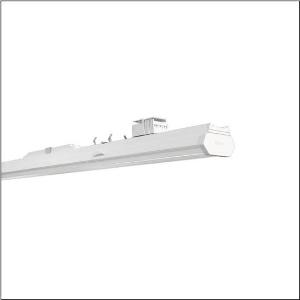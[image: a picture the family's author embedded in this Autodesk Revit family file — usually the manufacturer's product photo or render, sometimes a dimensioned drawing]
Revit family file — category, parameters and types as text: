
# Revit family: licross_11_protected_mo_51tp11dn685g
name_source: partatom
category: Lighting Fixtures
units: mm (PartAtom-declared; Revit-internal decimal feet)

## family parameters
Cut with Voids When Loaded = No
Host = Face
Light Source = No
Part Type = Normal
Room Calculation Point = No
Round Connector Dimension = Use Diameter
Shared = No

## types (1)
- --- (1 x LED, 8870 lm, 51.8 W, 6500K)
    Apparent Load = 52 VA
    CIE Flux Codes = 83 94 98 100 100
    Color Rendering = 80
    Color Temperature = 6500K
    Default Elevation = 1800 mm
    Description = Licross 11 Protected MO, luminaire insert, of sheet steel, galvanised, coil coated, white, length: 1.500mm, width: 90mm, height: 101mm, LED rated luminous flux: 8.870lm, light colour: 865, SDCM (Standard Deviation of Colour Matching)MacAdam ≤ 2 SDCM (initial), control gear: DALI 2, with plug, 5-pole, with phase selection, mains connection: 220..240V, AC, 50/60Hz, rated input power: 52W, internal wiring halogen-free, primary light control with lens, of plastic, primary optical cover: cover, of PMMA, light emission: direct distribution, primary light characteristic: symmetric, protection rating (complete): IP64, insulation class (complete): insulation class I (protective earthing), certification: CE, ENEC, VDE, UKCA, protection symbol: D if used in an environment with conductive dust loads with corresponding accessories, impact resistance: IK06, permissible ambient temperature for indoor applications: -25..+35°C, LABS conformity tested according to VDMA 24364:2018-05, reducing of maximum allowable ambient temperature of 5°C with ceiling mounting, corresponds to IFS (International Featured Standards) requirements for safety and quality in the food industry, The light source and the operating device comply with the requirements of the Ecodesign Regulation (EU) 2019/2020 and are replaceable in accordance with this regulation, packaging unit: 1 piece
    Height = 92 mm
    Lamp = 1 x LED
    Lamp Light Flux = 8870 lm
    Lamp Power = 51.8 W
    Lamp count = 1
    Length = 1500 mm
    Luminous efficacy = 171 lm/W
    Manufacturer = Siteco
    ModVariant = No
    Model = 51TP11DN685G
    Mounting Place = Ceiling
    Mounting Type = Pendant
    Number of Poles = 1
    OnlyDefault = Yes
    Power Factor = 1
    Product Name = Licross 11 Protected MO
    Product group = luminaire insert | ceiling pendant
    ProductGroupID = 901
    Protection Class = Protection class I
    Protection Degree = IP 64
    RLX_Detail_Level = 1
    RLX_Emergency_Light_Flux = 0 lm
    RLX_Emergency_Type = 0
    RLX_Emergency_Type_DB = No
    RlxData = <blob elided: 24445 chars, md5=29ec7273>
    Socket = socket
    Standby Power = 0 W
    System Light Flux = 8870 lm
    System Power = 52 W
    Type Comments = factory setting: luminous flux: 100 % | dim-lin: 254 | 344 mA
    Type Image = l_1256148.jpg
    URL = http://relux.com
    VarID = @adj_006439
    Voltage = 0 V
    Weight = 0.00 kg
    Width = 88 mm

## geometry (parser evidence)
native form markers: Blend x4, Sweep x10
no freeform markers — native parametric forms only
